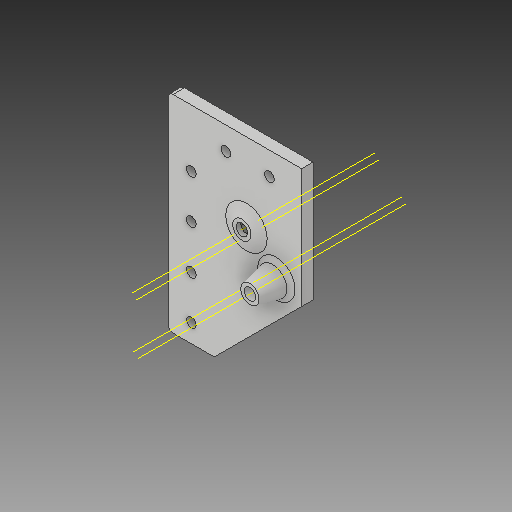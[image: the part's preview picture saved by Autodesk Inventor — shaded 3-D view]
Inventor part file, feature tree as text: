
AUTODESK INVENTOR PART (.ipt)
format: ipt  version: 2018 (Build 220112000, 112)  size: 216,064 bytes
history: native  units: in
note: dims shown in document units (in); Inventor stores cm internally (conversion verified against a paired STEP export)
features: sketch x8, extrude x6, plane x4, revolve x2, fillet x2, projected_geometry x2
ambient origin geometry x8: Origin, YZ Plane, XZ Plane, XY Plane, X Axis, Y Axis, Z Axis, Center Point
bodies: Solid1 (feature_tree)
feature tree (24):
  extrude  "Extrusion1"  Depth=0.7874in
  extrude  "Extrusion2"  Depth=3.5433in
  plane  "Work Plane2"
  revolve  "Revolution1"  [1 undecoded]
  extrude  "Extrusion3"  Depth=0.5118in
  extrude  "Extrusion4"  [1 undecoded]
  extrude  "Extrusion5"  Depth=0.0787in
  plane  "Work Plane4"
  revolve  "Revolution2"  [1 undecoded]
  fillet  "Fillet2"  Radius=0.1575in
  fillet  "Fillet3"  Radius=0.1654in
  extrude  "Extrusion6"  Depth=0.3937in
  sketch  "Sketch1"  dims[d0=0.7874in d1=0.7874in]
  sketch  "Sketch2"  dims[d2=3.5433in d3=3.5433in]
  plane  "Work Plane1"
  sketch  "Sketch3"  dims[d4=0.1969in d5=0.0in d6=0.1969in]
  sketch  "Sketch4"  dims[d7=1.3386in d8=0.5118in]
  projected_geometry  "Projected Loop1"
  sketch  "Sketch5"  dims[d9=0.2362in d10=0.0in d11=-0.0984in]
  sketch  "Sketch7"  dims[d12=0.3543in d13=0.0787in]
  plane  "Work Plane3"
  sketch  "Sketch8"  dims[d14=90.0deg d15=0.2362in d16=0.0in d17=0.1575in d18=0.1654in]
  projected_geometry  "Projected Loop2"
  sketch  "Sketch9"  dims[d19=0.315in d20=0.748in d21=0.748in d22=0.748in d23=0.315in d24=0.748in d25=0.748in d26=0.748in d27=0.2362in d28=0.0in d30=0.3268in d32=0.3268in d33=0.1969in d34=0.0in d35=0.0984in d36=0.1575in d37=0.0591in d38=0.4528in d39=90.0deg d40=0.0787in d41=0.0787in d42=1.2598in d43=0.3937in d44=0.0in]
note: 3 required parameter values undecoded (feature->parameter linkage not recoverable at this tier; creation-order binding heuristic only, values carry confidence <= 0.55)